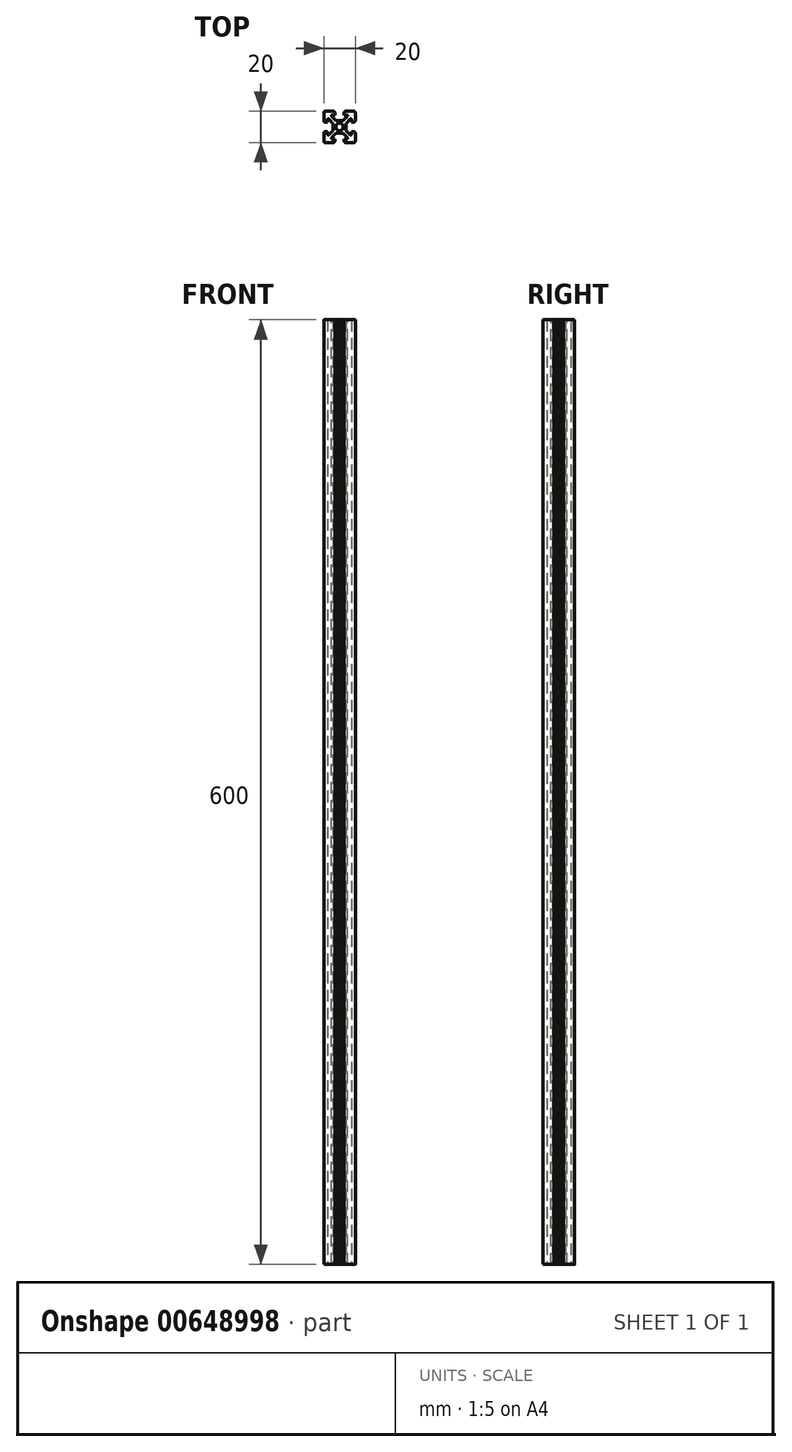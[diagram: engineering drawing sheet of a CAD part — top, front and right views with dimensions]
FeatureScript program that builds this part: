
annotation { "Feature Type Name" : "Feature", "Feature Type Description" : "" }
export const myFeature = defineFeature(function(context is Context, id is Id, definition is map)
    precondition{}
    {
        {
            var Q0;
            Q0=qCreatedBy(makeId("Top.planeOp"),FACE);
            var sketch = newSketch(context, id + "F0", { "sketchPlane" : qUnion([Q0])});
            skLineSegment(sketch, "E0", {"start": v(-15.81, 0) * mm, "end": v(2.4, 0) * mm, "construction": true});
            skLineSegment(sketch, "E1", {"start": v(0, 15.89) * mm, "end": v(0, -13.7) * mm, "construction": true});
            skLineSegment(sketch, "E2", {"start": v(0, 0) * mm, "end": v(-1.66, 1.66) * mm, "construction": true});
            skLineSegment(sketch, "E3", {"start": v(-2.3, 4.06) * mm, "end": v(-5.86, 7.63) * mm});
            skLineSegment(sketch, "E4", {"start": v(-5.86, 7.63) * mm, "end": v(-3, 7.63) * mm});
            skLineSegment(sketch, "E5", {"start": v(-3, 7.63) * mm, "end": v(-3, 10) * mm});
            skLineSegment(sketch, "E6", {"start": v(-3, 10) * mm, "end": v(-10, 10) * mm});
            skLineSegment(sketch, "E7.MirrorCS", {"start": v(-4, 2.23) * mm, "end": v(-7.63, 5.86) * mm});
            skLineSegment(sketch, "E8.MirrorCS", {"start": v(-7.63, 3) * mm, "end": v(-10, 3) * mm});
            skLineSegment(sketch, "E9.MirrorCS", {"start": v(-10, 3) * mm, "end": v(-10, 10) * mm});
            skLineSegment(sketch, "E10.MirrorCS", {"start": v(-7.63, 5.86) * mm, "end": v(-7.63, 3) * mm});
            skLineSegment(sketch, "E11.MirrorCS", {"start": v(3, 10) * mm, "end": v(10, 10) * mm});
            skLineSegment(sketch, "E12.MirrorCS", {"start": v(5.86, 7.63) * mm, "end": v(3, 7.63) * mm});
            skLineSegment(sketch, "E13.MirrorCS", {"start": v(3, 7.63) * mm, "end": v(3, 10) * mm});
            skLineSegment(sketch, "E14.MirrorCS", {"start": v(7.63, 5.86) * mm, "end": v(7.63, 3) * mm});
            skLineSegment(sketch, "E15.MirrorCS", {"start": v(10, 3) * mm, "end": v(10, 10) * mm});
            skLineSegment(sketch, "E16.MirrorCS", {"start": v(7.63, 3) * mm, "end": v(10, 3) * mm});
            skLineSegment(sketch, "E17.MirrorCS", {"start": v(2.3, 4.06) * mm, "end": v(5.86, 7.63) * mm});
            skLineSegment(sketch, "E18.MirrorCS", {"start": v(4, 2.23) * mm, "end": v(7.63, 5.86) * mm});
            skLineSegment(sketch, "E19.MirrorCS", {"start": v(5.86, -7.63) * mm, "end": v(3, -7.63) * mm});
            skLineSegment(sketch, "E20.MirrorCS", {"start": v(3, -10) * mm, "end": v(10, -10) * mm});
            skLineSegment(sketch, "E21.MirrorCS", {"start": v(-5.86, -7.63) * mm, "end": v(-3, -7.63) * mm});
            skLineSegment(sketch, "E22.MirrorCS", {"start": v(-3, -10) * mm, "end": v(-10, -10) * mm});
            skLineSegment(sketch, "E23.MirrorCS", {"start": v(-3, -7.63) * mm, "end": v(-3, -10) * mm});
            skLineSegment(sketch, "E24.MirrorCS", {"start": v(3, -7.63) * mm, "end": v(3, -10) * mm});
            skLineSegment(sketch, "E25.MirrorCS", {"start": v(7.63, -5.86) * mm, "end": v(7.63, -3) * mm});
            skLineSegment(sketch, "E26.MirrorCS", {"start": v(10, -3) * mm, "end": v(10, -10) * mm});
            skLineSegment(sketch, "E27.MirrorCS", {"start": v(4, -2.23) * mm, "end": v(7.63, -5.86) * mm});
            skLineSegment(sketch, "E28.MirrorCS", {"start": v(-7.63, -5.86) * mm, "end": v(-7.63, -3) * mm});
            skLineSegment(sketch, "E29.MirrorCS", {"start": v(-10, -3) * mm, "end": v(-10, -10) * mm});
            skLineSegment(sketch, "E30.MirrorCS", {"start": v(-7.63, -3) * mm, "end": v(-10, -3) * mm});
            skLineSegment(sketch, "E31.MirrorCS", {"start": v(-4, -2.23) * mm, "end": v(-7.63, -5.86) * mm});
            skLineSegment(sketch, "E32.MirrorCS", {"start": v(2.23, -4) * mm, "end": v(5.86, -7.63) * mm});
            skLineSegment(sketch, "E33.MirrorCS", {"start": v(-2.23, -4) * mm, "end": v(-5.86, -7.63) * mm});
            skLineSegment(sketch, "E34.MirrorCS", {"start": v(7.63, -3) * mm, "end": v(10, -3) * mm});
            skLineSegment(sketch, "E35", {"start": v(-4, 0) * mm, "end": v(-4, 0) * mm});
            skLineSegment(sketch, "E36", {"start": v(-2.3, 4.06) * mm, "end": v(-0.02, 4.06) * mm});
            skLineSegment(sketch, "E37.MirrorCS", {"start": v(-15.81, 8.12) * mm, "end": v(21.32, 8.12) * mm, "construction": true});
            skLineSegment(sketch, "E38", {"start": v(-4, 2.23) * mm, "end": v(-4, 0.02) * mm});
            skLineSegment(sketch, "E39", {"start": v(-2.23, -4) * mm, "end": v(-0.05, -4) * mm});
            skLineSegment(sketch, "E40", {"start": v(4, 2.23) * mm, "end": v(4, 0.03) * mm});
            skPoint(sketch, "E41.orphan", {"position": v(-0.59, 2.36) * mm});
            skPoint(sketch, "E42.orphan", {"position": v(-2.36, 0.59) * mm});
            skLineSegment(sketch, "E43.trimOffspring", {"start": v(0.03, 4.06) * mm, "end": v(2.3, 4.06) * mm});
            skPoint(sketch, "E44.orphan", {"position": v(0.59, 2.36) * mm});
            skPoint(sketch, "E45.orphan", {"position": v(2.36, 0.59) * mm});
            skPoint(sketch, "E46.orphan", {"position": v(-2.36, -0.59) * mm});
            skPoint(sketch, "E47.orphan", {"position": v(-0.59, -2.36) * mm});
            skPoint(sketch, "E48.orphan", {"position": v(0.59, -2.36) * mm});
            skPoint(sketch, "E49.orphan", {"position": v(2.36, -0.59) * mm});
            skLineSegment(sketch, "E50", {"start": v(-2.4, 0.03) * mm, "end": v(-2.4, 0.03) * mm});
            skLineSegment(sketch, "E51.MirrorCS", {"start": v(-2.4, -0.03) * mm, "end": v(-2.4, -0.03) * mm});
            skLineSegment(sketch, "E52.MirrorCS", {"start": v(2.4, 0.03) * mm, "end": v(2.4, 0.03) * mm});
            skLineSegment(sketch, "E53.MirrorCS", {"start": v(2.4, -0.03) * mm, "end": v(2.4, -0.03) * mm});
            skLineSegment(sketch, "E54.trimOffspring", {"start": v(4, -0.03) * mm, "end": v(4, -2.23) * mm});
            skLineSegment(sketch, "E55.trimOffspring", {"start": v(-4, -0.03) * mm, "end": v(-4, -2.23) * mm});
            skPoint(sketch, "E56.end.orphan", {"position": v(-2.4, 0) * mm});
            skPoint(sketch, "E57.orphan", {"position": v(-4, 0.03) * mm});
            skPoint(sketch, "E58.MirrorCS.end.orphan", {"position": v(2.4, 0) * mm});
            skPoint(sketch, "E58.MirrorCS.start.orphan", {"position": v(2.4, -0.03) * mm});
            skPoint(sketch, "E59.MirrorCS.start.orphan", {"position": v(2.4, 0.03) * mm});
            skLineSegment(sketch, "E60.trimOffspring", {"start": v(0.05, -4) * mm, "end": v(2.23, -4) * mm});
            skLineSegment(sketch, "E61", {"start": v(0, 0) * mm, "end": v(10, 10) * mm, "construction": true});
            skLineSegment(sketch, "E62", {"start": v(0, 0) * mm, "end": v(-10, -10) * mm, "construction": true});
            skLineSegment(sketch, "E63", {"start": v(10, -10) * mm, "end": v(0.07, 0.07) * mm, "construction": true});
            skPoint(sketch, "E64.start.orphan", {"position": v(-4, -0.03) * mm});
            skLineSegment(sketch, "E65", {"start": v(-2.82, -0.78) * mm, "end": v(-1.9, -1.37) * mm});
            skPoint(sketch, "E66.orphan", {"position": v(-1.66, -1.66) * mm});
            skPoint(sketch, "E67.orphan", {"position": v(0.03, -4.06) * mm});
            skPoint(sketch, "E68.orphan", {"position": v(-0.03, -4.06) * mm});
            skLineSegment(sketch, "E69", {"start": v(-2.82, 0.8) * mm, "end": v(-1.87, 1.41) * mm});
            skLineSegment(sketch, "E70", {"start": v(-0.76, 2.95) * mm, "end": v(-1.54, 1.77) * mm});
            skLineSegment(sketch, "E71", {"start": v(0.76, 2.95) * mm, "end": v(1.51, 1.8) * mm});
            skLineSegment(sketch, "E72", {"start": v(2.82, 0.8) * mm, "end": v(1.83, 1.46) * mm});
            skLineSegment(sketch, "E73", {"start": v(2.82, -0.8) * mm, "end": v(1.87, -1.41) * mm});
            skLineSegment(sketch, "E74.trimOffspring", {"start": v(1.8, -1.68) * mm, "end": v(1.82, -1.66) * mm});
            skLineSegment(sketch, "E75.trimOffspring", {"start": v(-8.12, 8.12) * mm, "end": v(-29.35, 29.35) * mm, "construction": true});
            skLineSegment(sketch, "E76", {"start": v(0.74, -2.96) * mm, "end": v(1.51, -1.8) * mm});
            skPoint(sketch, "E77.trimOffspring.start.orphan", {"position": v(0.33, -2.4) * mm});
            skPoint(sketch, "E78.MirrorCS.end.orphan", {"position": v(-0.33, -2.4) * mm});
            skLineSegment(sketch, "E79.trimOffspring", {"start": v(2.43, 0) * mm, "end": v(21.32, 0) * mm, "construction": true});
            skPoint(sketch, "E80.trimOffspring.start.orphan", {"position": v(0.33, 2.4) * mm});
            skPoint(sketch, "E81.trimOffspring.start.orphan", {"position": v(-0.33, 2.4) * mm});
            skArc(sketch, "E82", {"start": v(-1.87, 1.41) * mm, "mid": v(-2.35, 0.03) * mm, "end": v(-1.9, -1.37) * mm});
            skArc(sketch, "E83.trimOffspring", {"start": v(1.51, 1.8) * mm, "mid": v(-0.02, 2.35) * mm, "end": v(-1.54, 1.77) * mm});
            skArc(sketch, "E84.trimOffspring", {"start": v(1.87, -1.41) * mm, "mid": v(2.35, 0.03) * mm, "end": v(1.83, 1.46) * mm});
            skArc(sketch, "E85.trimOffspring", {"start": v(-1.55, -1.76) * mm, "mid": v(-0.03, -2.35) * mm, "end": v(1.51, -1.8) * mm});
            skLineSegment(sketch, "E86", {"start": v(-1.55, -1.76) * mm, "end": v(-0.75, -2.96) * mm});
            skLineSegment(sketch, "E87", {"start": v(-4, 0.03) * mm, "end": v(-2.82, 0.03) * mm});
            skLineSegment(sketch, "E88", {"start": v(-2.82, 0.03) * mm, "end": v(-2.82, 0.8) * mm});
            skLineSegment(sketch, "E89", {"start": v(-4, -0.03) * mm, "end": v(-2.82, -0.03) * mm});
            skLineSegment(sketch, "E90", {"start": v(-2.82, -0.03) * mm, "end": v(-2.82, -0.78) * mm});
            skLineSegment(sketch, "E91.MirrorCS", {"start": v(4, 0.03) * mm, "end": v(2.82, 0.03) * mm});
            skLineSegment(sketch, "E92.MirrorCS", {"start": v(4, -0.03) * mm, "end": v(2.82, -0.03) * mm});
            skLineSegment(sketch, "E93", {"start": v(2.82, 0.03) * mm, "end": v(2.82, 0.8) * mm});
            skLineSegment(sketch, "E94", {"start": v(2.82, -0.03) * mm, "end": v(2.82, -0.8) * mm});
            skLineSegment(sketch, "E95", {"start": v(-0.05, -4) * mm, "end": v(-0.05, -2.96) * mm});
            skLineSegment(sketch, "E96", {"start": v(-0.05, -2.96) * mm, "end": v(-0.75, -2.96) * mm});
            skLineSegment(sketch, "E97", {"start": v(0.05, -4) * mm, "end": v(0.05, -2.96) * mm});
            skLineSegment(sketch, "E98", {"start": v(0.05, -2.96) * mm, "end": v(0.74, -2.96) * mm});
            skLineSegment(sketch, "E99", {"start": v(-0.02, 4.06) * mm, "end": v(-0.02, 2.95) * mm});
            skLineSegment(sketch, "E100", {"start": v(-0.02, 2.95) * mm, "end": v(-0.76, 2.95) * mm});
            skLineSegment(sketch, "E101", {"start": v(0.03, 4.06) * mm, "end": v(0.03, 2.95) * mm});
            skLineSegment(sketch, "E102", {"start": v(0.03, 2.95) * mm, "end": v(0.76, 2.95) * mm});
            skSolve(sketch);
        }
        {
            var Q0;
            Q0=qSketchRegion(id+"F0",true);
            extrude(context, id + "F1", {"entities" : qUnion([Q0]), "depth" : 600 * mm, "offsetDistance" : 25.4 * mm});
        }
        {
            var Q0;
            Q0=makeQuery(id+"F1.opExtrude","SWEPT_EDGE",EDGE,{"disambiguationData":[OSD([sQuery(id+"F0.wireOp",EDGE,"E15.MirrorCS"),sQuery(id+"F0.wireOp",EDGE,"E11.MirrorCS")])]});
            var Q1;
            Q1=makeQuery(id+"F1.opExtrude","SWEPT_EDGE",EDGE,{"disambiguationData":[OSD([sQuery(id+"F0.wireOp",EDGE,"E20.MirrorCS"),sQuery(id+"F0.wireOp",EDGE,"E26.MirrorCS")])]});
            var Q2;
            Q2=makeQuery(id+"F1.opExtrude","SWEPT_EDGE",EDGE,{"disambiguationData":[OSD([sQuery(id+"F0.wireOp",EDGE,"E22.MirrorCS"),sQuery(id+"F0.wireOp",EDGE,"E29.MirrorCS")])]});
            var Q3;
            Q3=makeQuery(id+"F1.opExtrude","SWEPT_EDGE",EDGE,{"disambiguationData":[OSD([sQuery(id+"F0.wireOp",EDGE,"E22.MirrorCS"),sQuery(id+"F0.wireOp",EDGE,"E23.MirrorCS")])]});
            var Q4;
            Q4=makeQuery(id+"F1.opExtrude","SWEPT_EDGE",EDGE,{"disambiguationData":[OSD([sQuery(id+"F0.wireOp",EDGE,"E20.MirrorCS"),sQuery(id+"F0.wireOp",EDGE,"E24.MirrorCS")])]});
            var Q5;
            Q5=makeQuery(id+"F1.opExtrude","SWEPT_EDGE",EDGE,{"disambiguationData":[OSD([sQuery(id+"F0.wireOp",EDGE,"E5"),sQuery(id+"F0.wireOp",EDGE,"E6")])]});
            var Q6;
            Q6=makeQuery(id+"F1.opExtrude","SWEPT_EDGE",EDGE,{"disambiguationData":[OSD([sQuery(id+"F0.wireOp",EDGE,"E8.MirrorCS"),sQuery(id+"F0.wireOp",EDGE,"E9.MirrorCS")])]});
            var Q7;
            Q7=makeQuery(id+"F1.opExtrude","SWEPT_EDGE",EDGE,{"disambiguationData":[OSD([sQuery(id+"F0.wireOp",EDGE,"E15.MirrorCS"),sQuery(id+"F0.wireOp",EDGE,"E16.MirrorCS")])]});
            var Q8;
            Q8=makeQuery(id+"F1.opExtrude","SWEPT_EDGE",EDGE,{"disambiguationData":[OSD([sQuery(id+"F0.wireOp",EDGE,"E26.MirrorCS"),sQuery(id+"F0.wireOp",EDGE,"E34.MirrorCS")])]});
            var Q9;
            Q9=makeQuery(id+"F1.opExtrude","SWEPT_EDGE",EDGE,{"disambiguationData":[OSD([sQuery(id+"F0.wireOp",EDGE,"E29.MirrorCS"),sQuery(id+"F0.wireOp",EDGE,"E30.MirrorCS")])]});
            var Q10;
            Q10=makeQuery(id+"F1.opExtrude","SWEPT_EDGE",EDGE,{"disambiguationData":[OSD([sQuery(id+"F0.wireOp",EDGE,"E9.MirrorCS"),sQuery(id+"F0.wireOp",EDGE,"E6")])]});
            var Q11;
            Q11=makeQuery(id+"F1.opExtrude","SWEPT_EDGE",EDGE,{"disambiguationData":[OSD([sQuery(id+"F0.wireOp",EDGE,"E13.MirrorCS"),sQuery(id+"F0.wireOp",EDGE,"E11.MirrorCS")])]});
            fillet(context, id + "F2", {"entities" : qUnion([Q0, Q1, Q2, Q3, Q4, Q5, Q6, Q7, Q8, Q9, Q10, Q11]), "radius" : 1 * mm, "tangentPropagation" : true, "allowEdgeOverflow" : false});
        }
        {
            var Q0;
            Q0=makeQuery(id+"F1.opExtrude","SWEPT_EDGE",EDGE,{"disambiguationData":[OSD([sQuery(id+"F0.wireOp",EDGE,"E7.MirrorCS"),sQuery(id+"F0.wireOp",EDGE,"E10.MirrorCS")])]});
            var Q1;
            Q1=makeQuery(id+"F1.opExtrude","SWEPT_EDGE",EDGE,{"disambiguationData":[OSD([sQuery(id+"F0.wireOp",EDGE,"E3"),sQuery(id+"F0.wireOp",EDGE,"E4")])]});
            var Q2;
            Q2=makeQuery(id+"F1.opExtrude","SWEPT_EDGE",EDGE,{"disambiguationData":[OSD([sQuery(id+"F0.wireOp",EDGE,"E12.MirrorCS"),sQuery(id+"F0.wireOp",EDGE,"E17.MirrorCS")])]});
            var Q3;
            Q3=makeQuery(id+"F1.opExtrude","SWEPT_EDGE",EDGE,{"disambiguationData":[OSD([sQuery(id+"F0.wireOp",EDGE,"E14.MirrorCS"),sQuery(id+"F0.wireOp",EDGE,"E18.MirrorCS")])]});
            var Q4;
            Q4=makeQuery(id+"F1.opExtrude","SWEPT_EDGE",EDGE,{"disambiguationData":[OSD([sQuery(id+"F0.wireOp",EDGE,"E28.MirrorCS"),sQuery(id+"F0.wireOp",EDGE,"E31.MirrorCS")])]});
            var Q5;
            Q5=makeQuery(id+"F1.opExtrude","SWEPT_EDGE",EDGE,{"disambiguationData":[OSD([sQuery(id+"F0.wireOp",EDGE,"E21.MirrorCS"),sQuery(id+"F0.wireOp",EDGE,"E33.MirrorCS")])]});
            var Q6;
            Q6=makeQuery(id+"F1.opExtrude","SWEPT_EDGE",EDGE,{"disambiguationData":[OSD([sQuery(id+"F0.wireOp",EDGE,"E19.MirrorCS"),sQuery(id+"F0.wireOp",EDGE,"E32.MirrorCS")])]});
            var Q7;
            Q7=makeQuery(id+"F1.opExtrude","SWEPT_EDGE",EDGE,{"disambiguationData":[OSD([sQuery(id+"F0.wireOp",EDGE,"E25.MirrorCS"),sQuery(id+"F0.wireOp",EDGE,"E27.MirrorCS")])]});
            fillet(context, id + "F3", {"entities" : qUnion([Q0, Q1, Q2, Q3, Q4, Q5, Q6, Q7]), "radius" : .5 * mm, "tangentPropagation" : true, "allowEdgeOverflow" : false});
        }
        {
            var Q0;
            Q0=makeQuery(id+"F1.opExtrude","SWEPT_EDGE",EDGE,{"disambiguationData":[OSD([sQuery(id+"F0.wireOp",EDGE,"E69"),sQuery(id+"F0.wireOp",EDGE,"E82")])]});
            var Q1;
            Q1=makeQuery(id+"F1.opExtrude","SWEPT_EDGE",EDGE,{"disambiguationData":[OSD([sQuery(id+"F0.wireOp",EDGE,"E17.MirrorCS"),sQuery(id+"F0.wireOp",EDGE,"E43.trimOffspring")])]});
            var Q2;
            {var subQ0=sQuery(id+"F0.wireOp",EDGE,"E12.MirrorCS");Q2=makeQuery(id+"F3.opFillet","BLEND_EDGE",EDGE,{"blendedFrom":[makeQuery(id+"F1.opExtrude","SWEPT_EDGE",EDGE,{"disambiguationData":[OSD([subQ0,sQuery(id+"F0.wireOp",EDGE,"E17.MirrorCS")])]}),makeQuery(id+"F1.opExtrude","SWEPT_FACE",FACE,{"disambiguationData":[OSD([subQ0])]})],"blendedInto":[makeQuery(id+"F1.opExtrude","SWEPT_FACE",FACE,{"disambiguationData":[OSD([subQ0])]})]});}
            var Q3;
            Q3=makeQuery(id+"F1.opExtrude","SWEPT_EDGE",EDGE,{"disambiguationData":[OSD([sQuery(id+"F0.wireOp",EDGE,"E70"),sQuery(id+"F0.wireOp",EDGE,"E83.trimOffspring")])]});
            var Q4;
            Q4=makeQuery(id+"F1.opExtrude","SWEPT_EDGE",EDGE,{"disambiguationData":[OSD([sQuery(id+"F0.wireOp",EDGE,"VnvyymTW-JKNP-Vp1J-SOXt-zXPDHYCny5Fm"),sQuery(id+"F0.wireOp",EDGE,"E85.trimOffspring")])]});
            var Q5;
            Q5=makeQuery(id+"F1.opExtrude","SWEPT_EDGE",EDGE,{"disambiguationData":[OSD([sQuery(id+"F0.wireOp",EDGE,"E76"),sQuery(id+"F0.wireOp",EDGE,"E85.trimOffspring")])]});
            var Q6;
            Q6=makeQuery(id+"F1.opExtrude","SWEPT_EDGE",EDGE,{"disambiguationData":[OSD([sQuery(id+"F0.wireOp",EDGE,"E73"),sQuery(id+"F0.wireOp",EDGE,"E84.trimOffspring")])]});
            var Q7;
            Q7=makeQuery(id+"F1.opExtrude","SWEPT_EDGE",EDGE,{"disambiguationData":[OSD([sQuery(id+"F0.wireOp",EDGE,"E72"),sQuery(id+"F0.wireOp",EDGE,"E84.trimOffspring")])]});
            var Q8;
            Q8=makeQuery(id+"F1.opExtrude","SWEPT_EDGE",EDGE,{"disambiguationData":[OSD([sQuery(id+"F0.wireOp",EDGE,"E71"),sQuery(id+"F0.wireOp",EDGE,"E83.trimOffspring")])]});
            var Q9;
            Q9=makeQuery(id+"F1.opExtrude","SWEPT_EDGE",EDGE,{"disambiguationData":[OSD([sQuery(id+"F0.wireOp",EDGE,"E65"),sQuery(id+"F0.wireOp",EDGE,"E82")])]});
            fillet(context, id + "F4", {"entities" : qUnion([Q0, Q1, Q2, Q3, Q4, Q5, Q6, Q7, Q8, Q9]), "radius" : .1 * mm, "tangentPropagation" : true, "allowEdgeOverflow" : false});
        }
    });
